# Revit family: HVAC_HangingSystems_Walraven_BIS_RapidStrut_Slide_Nut_with_Plastic_Tabs_(BUP1000)
name_source: partatom
category: Mechanical Equipment
revit_build: Autodesk Revit MEP 2016 (Build: 20150220_1215(x64)
units: mm (PartAtom-declared; Revit-internal decimal feet)

## family parameters
Always vertical = No
Cut with Voids When Loaded = No
OmniClass Number = 23.60.30.11.17
OmniClass Title = Pipework/Ductwork Mechanical Fasteners/Supports
Part Type = Normal
Room Calculation Point = No
Round Connector Dimension = Use Diameter
Shared = No
Work Plane-Based = Yes

## types (4) — shared parameters
Assembly Code = 50
BIMobject category = Hanging Systems
BIMobject category code = hvac-hanging-systems
BIMobject main category = HVAC
BIMobject main category code = hvac
Brand url = https://www.walraven.com
Date of publishing = 7/20/2018
Description = slide nut with plastic tabs
Design country = Netherlands
IFC Classification = Mechanical Fastener
IfcDescription = slide nut with plastic tabs
IfcExportAs = IfcMechanicalFastenerType
IfcExportType = USERDEFINED
Manufacturer = Walraven
Manufacturer country = Netherlands
Manufacturer name = Walraven
Material main = Steel
Material secondary = Polypropylene
Model = BIS RapidStrut Slide Nut with Plastic Tabs (BUP1000)
NLRS_C_code_SfB_tabel1 = 50
NLRS_C_niveau_ontwikkeling = LOD400
OmniClass Code = 23-27 43 13
OmniClass Description = Mechanical Pipe Supports
Product Guid = ebcee931-a172-4643-a88d-50364ce17fa8
Product SKU = bis-rapidstrut-slide-nut-with-plastic-tabs-bup1000
Product data url = https://bimobject.com
Product family = Rail Systems
Product group = Slide Nuts
Product url = https://www.walraven.com
QR code = http://bimobject.com
RSen_C_code_ETIM = EC000096
RSen_C_code_ETIM_url = https://prod.etim-international.com
RSen_C_content_modification_date = 04-06-2018
RSen_C_content_releasedate = 04-06-2018
RSen_C_intended_use = hanging systems
RSen_C_material = steel
RSen_C_material_01 = polypropylene (PE)
RSen_C_material_colour = grey+green
RSen_C_material_finish = BIS UltraProtect® 1000
Technical description = https://library.walraven.com
URL = https://www.walraven.com
Weight Net (Kg) = 0
region_index = 1
zero-valued in all types: Edition number, Nominal height, Nominal width

## per-type parameters (varying)
| type | Default Elevation | type_index |
| M12 | 1219 mm | 4 |
| M10 | 2 mm  [stored 0.00656168 ft] | 3 |
| M8 | 1219 mm | 2 |
| M6 | 1219 mm | 1 |

note: [stored X ft] marks values corroborated as IEEE doubles in the binary element streams (Revit-internal decimal feet)

## geometry (parser evidence)
native form markers: Blend x2, Sweep x3
no freeform markers — native parametric forms only
